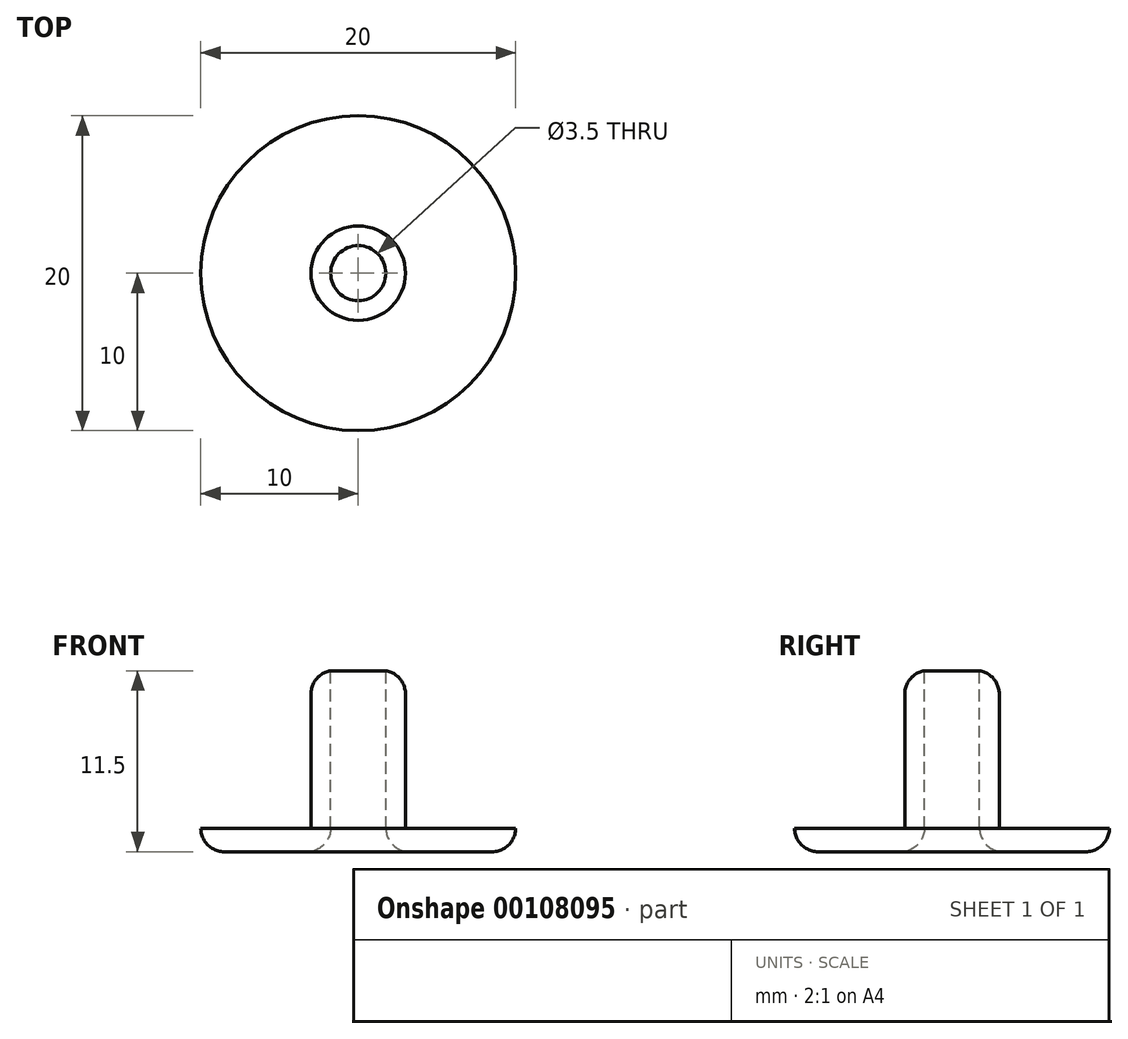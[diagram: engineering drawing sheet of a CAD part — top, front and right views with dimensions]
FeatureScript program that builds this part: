
annotation { "Feature Type Name" : "Feature", "Feature Type Description" : "" }
export const myFeature = defineFeature(function(context is Context, id is Id, definition is map)
    precondition{}
    {
        {
            var Q0;
            Q0=qCreatedBy(makeId("Top.planeOp"),FACE);
            var sketch = newSketch(context, id + "F0", { "sketchPlane" : qUnion([Q0])});
            skCircle(sketch, "E0", {"center": v(0, 0) * mm, "radius": 10 * mm});
            skSolve(sketch);
        }
        {
            var Q0;
            Q0 = qSketchRegion(id + "F0", true);
            extrude(context, id + "F1", {"entities" : qUnion([Q0]), "depth" : 1.5 * mm});
        }
        {
            var Q0;
            Q0=makeQuery(id+"F1.opExtrude","CAP_FACE",FACE,{"disambiguationData":[OSD([sQuery(id+"F0.wireOp",EDGE,"E0")])],"isStart":false});
            var sketch = newSketch(context, id + "F2", { "sketchPlane" : qUnion([Q0])});
            skCircle(sketch, "E1", {"center": v(0, 0) * mm, "radius": 3 * mm});
            skSolve(sketch);
        }
        {
            var Q0;
            Q0 = qSketchRegion(id + "F2", true);
            extrude(context, id + "F3", {"entities" : qUnion([Q0]), "operationType" : NewBodyOperationType.ADD, "depth" : 10 * mm});
        }
        {
            var Q0;
            Q0=makeQuery(id+"F3.opExtrude","CAP_FACE",FACE,{"disambiguationData":[OSD([sQuery(id+"F2.wireOp",EDGE,"E1")])],"isStart":false});
            var sketch = newSketch(context, id + "F4", { "sketchPlane" : qUnion([Q0])});
            skCircle(sketch, "E2", {"center": v(0, 0) * mm, "radius": 1.75 * mm});
            skSolve(sketch);
        }
        {
            var Q0;
            Q0 = qSketchRegion(id + "F4", true);
            extrude(context, id + "F5", {"entities" : qUnion([Q0]), "operationType" : NewBodyOperationType.REMOVE, "endBound" : BoundingType.THROUGH_ALL, "oppositeDirection" : true, "depth" : 25 * mm});
        }
        {
            var Q0;
            Q0=makeQuery(id+"F1.opExtrude","CAP_FACE",FACE,{"disambiguationData":[OSD([sQuery(id+"F0.wireOp",EDGE,"E0")])],"isStart":true});
            var Q1;
            Q1=makeQuery(id+"F3.opExtrude","CAP_EDGE",EDGE,{"disambiguationData":[OSD([sQuery(id+"F2.wireOp",EDGE,"E1")])],"isStart":false});
            fillet(context, id + "F6", {"entities" : qUnion([Q0, Q1]), "radius" : 1.5 * mm, "tangentPropagation" : true, "allowEdgeOverflow" : false});
        }
    });
